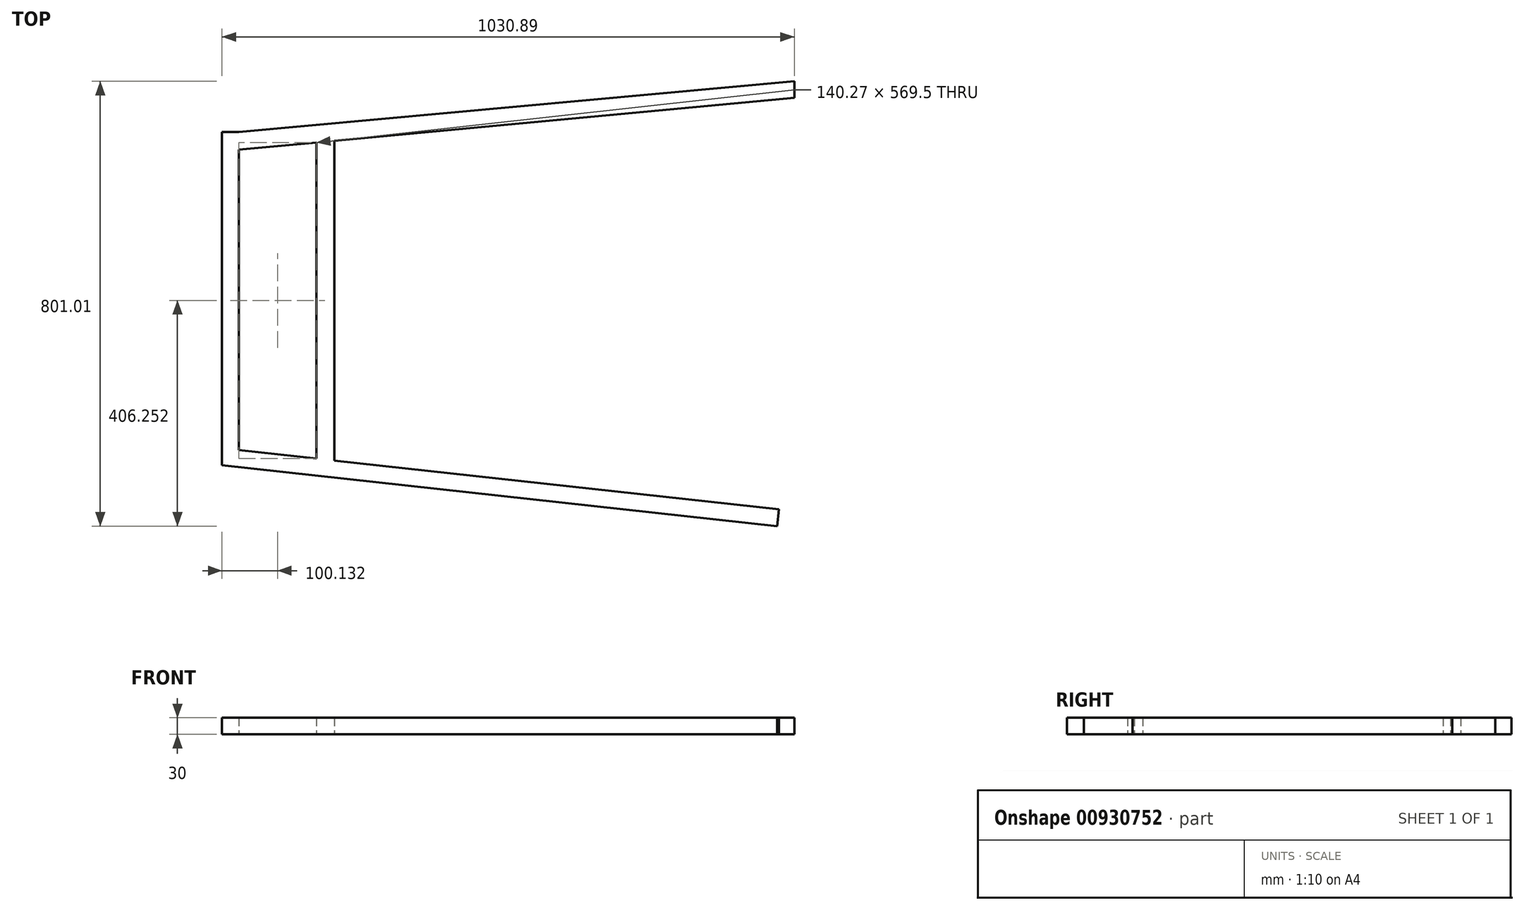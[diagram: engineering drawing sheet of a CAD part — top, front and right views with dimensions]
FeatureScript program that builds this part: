
annotation { "Feature Type Name" : "Feature", "Feature Type Description" : "" }
export const myFeature = defineFeature(function(context is Context, id is Id, definition is map)
    precondition{}
    {
        {
            var Q0;
            Q0=qCreatedBy(makeId("Top.planeOp"),FACE);
            var sketch = newSketch(context, id + "F0", { "sketchPlane" : qUnion([Q0])});
            skLineSegment(sketch, "E0.bottom", {"start": v(-75.58, 304.95) * mm, "end": v(-45.58, 304.95) * mm});
            skLineSegment(sketch, "E0.top", {"start": v(-75.58, -295.05) * mm, "end": v(-45.58, -295.05) * mm});
            skLineSegment(sketch, "E0.left", {"start": v(-75.58, 304.95) * mm, "end": v(-75.58, -295.05) * mm});
            skLineSegment(sketch, "E0.right", {"start": v(-45.58, 304.95) * mm, "end": v(-45.58, -295.05) * mm});
            skLineSegment(sketch, "E1", {"start": v(-75.58, -295.05) * mm, "end": v(924.42, -404.58) * mm});
            skLineSegment(sketch, "E2", {"start": v(924.42, -404.58) * mm, "end": v(927.73, -374.32) * mm});
            skLineSegment(sketch, "E3", {"start": v(927.73, -374.32) * mm, "end": v(-45.58, -267.71) * mm});
            skLineSegment(sketch, "E4", {"start": v(-45.58, 304.95) * mm, "end": v(955.3, 396.43) * mm});
            skLineSegment(sketch, "E5", {"start": v(955.3, 396.43) * mm, "end": v(955.3, 366.95) * mm});
            skLineSegment(sketch, "E6", {"start": v(955.3, 366.95) * mm, "end": v(-45.58, 273.3) * mm});
            skLineSegment(sketch, "E7", {"start": v(94.68, -283.08) * mm, "end": v(94.68, 286.42) * mm});
            skLineSegment(sketch, "E8", {"start": v(94.68, 286.42) * mm, "end": v(126.9, 289.43) * mm});
            skLineSegment(sketch, "E9", {"start": v(126.9, 289.43) * mm, "end": v(126.9, -286.6) * mm});
            skSolve(sketch);
        }
        {
            var Q0;
            {var subQ1=sQuery(id+"F0.wireOp",EDGE,"E0.bottom");Q0=makeQuery(id+"F0.imprint","IMPRINT",FACE,{"disambiguationData":[TD([[makeQuery(id+"F0.imprint","IMPRINT",EDGE,{"derivedFrom":subQ1}),-1.0]])]});}
            var Q1;
            {var subQ2=sQuery(id+"F0.wireOp",EDGE,"E0.top");Q1=makeQuery(id+"F0.imprint","IMPRINT",FACE,{"disambiguationData":[TD([[makeQuery(id+"F0.imprint","IMPRINT",EDGE,{"derivedFrom":subQ2}),-1.0]])]});}
            var Q2;
            {var subQ0=sQuery(id+"F0.wireOp",EDGE,"E7");Q2=makeQuery(id+"F0.imprint","IMPRINT",FACE,{"disambiguationData":[TD([[makeQuery(id+"F0.imprint","IMPRINT",EDGE,{"derivedFrom":subQ0}),-1.0]])]});}
            var Q3;
            {var subQ1=sQuery(id+"F0.wireOp",EDGE,"E4");Q3=makeQuery(id+"F0.imprint","IMPRINT",FACE,{"disambiguationData":[TD([[makeQuery(id+"F0.imprint","IMPRINT",EDGE,{"derivedFrom":subQ1}),-1.0]])]});}
            extrude(context, id + "F1", {"entities" : qUnion([Q0, Q1, Q2, Q3]), "depth" : 30 * mm, "offsetDistance" : 25 * mm});
        }
    });
